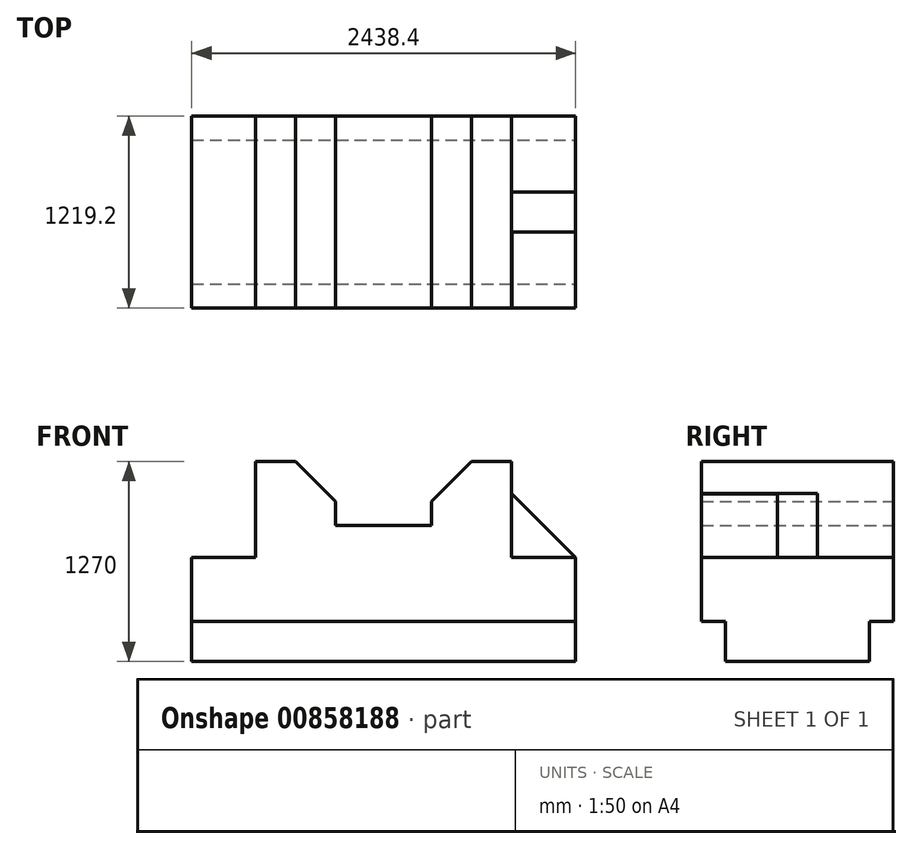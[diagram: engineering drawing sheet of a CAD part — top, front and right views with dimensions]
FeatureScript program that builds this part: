
annotation { "Feature Type Name" : "Feature", "Feature Type Description" : "" }
export const myFeature = defineFeature(function(context is Context, id is Id, definition is map)
    precondition{}
    {
        {
            var Q0;
            Q0=qCreatedBy(makeId("Front.planeOp"),FACE);
            var sketch = newSketch(context, id + "F0", { "sketchPlane" : qUnion([Q0])});
            skLineSegment(sketch, "E0.bottom", {"start": v(-1219.2, 635) * mm, "end": v(1219.2, 635) * mm});
            skLineSegment(sketch, "E0.top", {"start": v(-1219.2, -635) * mm, "end": v(1219.2, -635) * mm});
            skLineSegment(sketch, "E0.left", {"start": v(-1219.2, 635) * mm, "end": v(-1219.2, -635) * mm});
            skLineSegment(sketch, "E0.right", {"start": v(1219.2, 635) * mm, "end": v(1219.2, -635) * mm});
            skPoint(sketch, "E0.middle", {"position": v(0, 0) * mm});
            skLineSegment(sketch, "E1.bottom", {"start": v(1219.2, 635) * mm, "end": v(812.8, 635) * mm});
            skLineSegment(sketch, "E1.top", {"start": v(1219.2, -635) * mm, "end": v(812.8, -635) * mm});
            skLineSegment(sketch, "E1.right", {"start": v(812.8, 635) * mm, "end": v(812.8, -635) * mm});
            skLineSegment(sketch, "E2.top", {"start": v(1219.2, 25.4) * mm, "end": v(812.8, 25.4) * mm});
            skLineSegment(sketch, "E2.left", {"start": v(1219.2, -635) * mm, "end": v(1219.2, 25.4) * mm});
            skLineSegment(sketch, "E3.bottom", {"start": v(812.8, 635) * mm, "end": v(558.8, 635) * mm});
            skLineSegment(sketch, "E3.top", {"start": v(812.8, -635) * mm, "end": v(558.8, -635) * mm});
            skLineSegment(sketch, "E3.right", {"start": v(558.8, 635) * mm, "end": v(558.8, -635) * mm});
            skLineSegment(sketch, "E4.bottom", {"start": v(558.8, -635) * mm, "end": v(304.8, -635) * mm});
            skLineSegment(sketch, "E4.top", {"start": v(558.8, 635) * mm, "end": v(304.8, 635) * mm});
            skLineSegment(sketch, "E4.left", {"start": v(558.8, -635) * mm, "end": v(558.8, 635) * mm});
            skLineSegment(sketch, "E4.right", {"start": v(304.8, -635) * mm, "end": v(304.8, 635) * mm});
            skLineSegment(sketch, "E5.bottom", {"start": v(304.8, -635) * mm, "end": v(-304.8, -635) * mm});
            skLineSegment(sketch, "E5.top", {"start": v(304.8, 635) * mm, "end": v(-304.8, 635) * mm});
            skLineSegment(sketch, "E5.right", {"start": v(-304.8, -635) * mm, "end": v(-304.8, 635) * mm});
            skLineSegment(sketch, "E6.bottom", {"start": v(-1219.2, 635) * mm, "end": v(-812.8, 635) * mm});
            skLineSegment(sketch, "E6.top", {"start": v(-1219.2, -635) * mm, "end": v(-812.8, -635) * mm});
            skLineSegment(sketch, "E6.right", {"start": v(-812.8, 635) * mm, "end": v(-812.8, -635) * mm});
            skLineSegment(sketch, "E7.bottom", {"start": v(-812.8, 635) * mm, "end": v(-558.8, 635) * mm});
            skLineSegment(sketch, "E7.top", {"start": v(-812.8, -635) * mm, "end": v(-558.8, -635) * mm});
            skLineSegment(sketch, "E7.right", {"start": v(-558.8, 635) * mm, "end": v(-558.8, -635) * mm});
            skLineSegment(sketch, "E8.bottom", {"start": v(-812.8, -635) * mm, "end": v(-1219.2, -635) * mm});
            skLineSegment(sketch, "E8.top", {"start": v(-812.8, 25.4) * mm, "end": v(-1219.2, 25.4) * mm});
            skLineSegment(sketch, "E8.left", {"start": v(-812.8, -635) * mm, "end": v(-812.8, 25.4) * mm});
            skLineSegment(sketch, "E8.right", {"start": v(-1219.2, -635) * mm, "end": v(-1219.2, 25.4) * mm});
            skLineSegment(sketch, "E9.top", {"start": v(-812.8, 228.6) * mm, "end": v(-558.8, 228.6) * mm});
            skLineSegment(sketch, "E9.left", {"start": v(-812.8, 635) * mm, "end": v(-812.8, 228.6) * mm});
            skLineSegment(sketch, "E9.right", {"start": v(-558.8, 635) * mm, "end": v(-558.8, 228.6) * mm});
            skLineSegment(sketch, "E10", {"start": v(-558.8, 228.6) * mm, "end": v(304.8, 228.6) * mm});
            skLineSegment(sketch, "E11", {"start": v(-558.8, 228.6) * mm, "end": v(-152.4, 228.6) * mm});
            skLineSegment(sketch, "E12", {"start": v(-558.8, 635) * mm, "end": v(-152.4, 228.6) * mm});
            skLineSegment(sketch, "E13", {"start": v(812.8, 25.4) * mm, "end": v(812.8, 431.8) * mm});
            skLineSegment(sketch, "E14", {"start": v(812.8, 431.8) * mm, "end": v(1219.2, 25.4) * mm});
            skLineSegment(sketch, "E15", {"start": v(304.8, 635) * mm, "end": v(304.8, 381) * mm});
            skLineSegment(sketch, "E16", {"start": v(558.8, 635) * mm, "end": v(304.8, 381) * mm});
            skSolve(sketch);
        }
        {
            var Q0;
            {var subQ5=sQuery(id+"F0.wireOp",EDGE,"E8.top");Q0=makeQuery(id+"F0.imprint","IMPRINT",FACE,{"disambiguationData":[TD([[makeQuery(id+"F0.imprint","IMPRINT",EDGE,{"derivedFrom":subQ5}),1.0]])]});}
            var Q1;
            {var subQ2=sQuery(id+"F0.wireOp",EDGE,"E9.top");Q1=makeQuery(id+"F0.imprint","IMPRINT",FACE,{"disambiguationData":[TD([[makeQuery(id+"F0.imprint","IMPRINT",EDGE,{"derivedFrom":subQ2}),-1.0]])]});}
            var Q2;
            {var subQ5=sQuery(id+"F0.wireOp",EDGE,"E9.top");Q2=makeQuery(id+"F0.imprint","IMPRINT",FACE,{"disambiguationData":[TD([[makeQuery(id+"F0.imprint","IMPRINT",EDGE,{"derivedFrom":subQ5}),1.0]])]});}
            var Q3;
            {var subQ0=sQuery(id+"F0.wireOp",EDGE,"E12");var subQ1=sQuery(id+"F0.wireOp",EDGE,"E5.right");var subQ2=makeQuery(id+"F0.imprint","INTERSECT",VERTEX,{"derivedFrom":[subQ1,subQ0]});Q3=makeQuery(id+"F0.imprint","IMPRINT",FACE,{"disambiguationData":[TD([[makeQuery(id+"F0.imprint","IMPRINT",EDGE,{"disambiguationData":[TD([[subQ2,1.0]])],"derivedFrom":subQ1}),1.0]])]});}
            var Q4;
            {var subQ0=sQuery(id+"F0.wireOp",EDGE,"E5.right");var subQ1=sQuery(id+"F0.wireOp",EDGE,"E0.top");var subQ2=makeQuery(id+"F0.imprint","INTERSECT",VERTEX,{"derivedFrom":[subQ1,subQ0]});Q4=makeQuery(id+"F0.imprint","IMPRINT",FACE,{"disambiguationData":[TD([[makeQuery(id+"F0.imprint","IMPRINT",EDGE,{"disambiguationData":[TD([[subQ2,1.0]])],"derivedFrom":subQ1}),1.0]])]});}
            var Q5;
            {var subQ4=sQuery(id+"F0.wireOp",EDGE,"E5.right");var subQ5=sQuery(id+"F0.wireOp",EDGE,"E0.top");var subQ6=makeQuery(id+"F0.imprint","INTERSECT",VERTEX,{"derivedFrom":[subQ5,subQ4]});Q5=makeQuery(id+"F0.imprint","IMPRINT",FACE,{"disambiguationData":[TD([[makeQuery(id+"F0.imprint","IMPRINT",EDGE,{"disambiguationData":[TD([[subQ6,-1.0]])],"derivedFrom":subQ5}),1.0]])]});}
            var Q6;
            {var subQ4=sQuery(id+"F0.wireOp",EDGE,"E3.right");Q6=makeQuery(id+"F0.imprint","IMPRINT",FACE,{"disambiguationData":[TD([[makeQuery(id+"F0.imprint","IMPRINT",EDGE,{"derivedFrom":subQ4}),-1.0]])]});}
            var Q7;
            {var subQ5=sQuery(id+"F0.wireOp",EDGE,"E3.right");Q7=makeQuery(id+"F0.imprint","IMPRINT",FACE,{"disambiguationData":[TD([[makeQuery(id+"F0.imprint","IMPRINT",EDGE,{"derivedFrom":subQ5}),1.0]])]});}
            var Q8;
            {var subQ0=sQuery(id+"F0.wireOp",EDGE,"E2.top");Q8=makeQuery(id+"F0.imprint","IMPRINT",FACE,{"disambiguationData":[TD([[makeQuery(id+"F0.imprint","IMPRINT",EDGE,{"derivedFrom":subQ0}),-1.0]])]});}
            var Q9;
            {var subQ5=sQuery(id+"F0.wireOp",EDGE,"E2.top");Q9=makeQuery(id+"F0.imprint","IMPRINT",FACE,{"disambiguationData":[TD([[makeQuery(id+"F0.imprint","IMPRINT",EDGE,{"derivedFrom":subQ5}),1.0]])]});}
            extrude(context, id + "F1", {"entities" : qUnion([Q0, Q1, Q2, Q3, Q4, Q5, Q6, Q7, Q8, Q9]), "depth" : 1219.2 * mm, "offsetDistance" : 25.4 * mm});
        }
        {
            var Q0;
            Q0=makeQuery(id+"F1.opExtrude","SWEPT_FACE",FACE,{"disambiguationData":[OSD([sQuery(id+"F0.wireOp",EDGE,"E0.right")])]});
            var sketch = newSketch(context, id + "F2", { "sketchPlane" : qUnion([Q0])});
            skLineSegment(sketch, "E17.bottom", {"start": v(-1219.2, -635) * mm, "end": v(-1066.8, -635) * mm});
            skLineSegment(sketch, "E17.top", {"start": v(-1219.2, -381) * mm, "end": v(-1066.8, -381) * mm});
            skLineSegment(sketch, "E17.left", {"start": v(-1219.2, -635) * mm, "end": v(-1219.2, -381) * mm});
            skLineSegment(sketch, "E17.right", {"start": v(-1066.8, -635) * mm, "end": v(-1066.8, -381) * mm});
            skLineSegment(sketch, "E18.bottom", {"start": v(0, -635) * mm, "end": v(-152.4, -635) * mm});
            skLineSegment(sketch, "E18.top", {"start": v(0, -381) * mm, "end": v(-152.4, -381) * mm});
            skLineSegment(sketch, "E18.left", {"start": v(0, -635) * mm, "end": v(0, -381) * mm});
            skLineSegment(sketch, "E18.right", {"start": v(-152.4, -635) * mm, "end": v(-152.4, -381) * mm});
            skSolve(sketch);
        }
        {
            var Q0;
            Q0=makeQuery(id+"F2.imprint","IMPRINT",FACE,{"disambiguationData":[TD([[makeQuery(id+"F2.imprint","IMPRINT",EDGE,{"derivedFrom":sQuery(id+"F2.wireOp",EDGE,"E17.bottom")}),1.0]])]});
            var Q1;
            Q1=makeQuery(id+"F2.imprint","IMPRINT",FACE,{"disambiguationData":[TD([[makeQuery(id+"F2.imprint","IMPRINT",EDGE,{"derivedFrom":sQuery(id+"F2.wireOp",EDGE,"E18.bottom")}),1.0]])]});
            extrude(context, id + "F3", {"entities" : qUnion([Q0, Q1]), "operationType" : NewBodyOperationType.REMOVE, "oppositeDirection" : true, "depth" : 2438.4 * mm, "offsetDistance" : 25.4 * mm});
        }
        {
            var Q0;
            Q0=makeQuery(id+"F1.opExtrude","SWEPT_FACE",FACE,{"disambiguationData":[OSD([sQuery(id+"F0.wireOp",EDGE,"E0.right")])]});
            var sketch = newSketch(context, id + "F4", { "sketchPlane" : qUnion([Q0])});
            skLineSegment(sketch, "E19.bottom", {"start": v(-1219.2, 25.4) * mm, "end": v(-736.6, 25.4) * mm});
            skLineSegment(sketch, "E19.top", {"start": v(-1219.2, 430.42) * mm, "end": v(-736.6, 430.42) * mm});
            skLineSegment(sketch, "E19.left", {"start": v(-1219.2, 25.4) * mm, "end": v(-1219.2, 430.42) * mm});
            skLineSegment(sketch, "E19.right", {"start": v(-736.6, 25.4) * mm, "end": v(-736.6, 430.42) * mm});
            skLineSegment(sketch, "E20.bottom", {"start": v(0, 25.4) * mm, "end": v(-482.6, 25.4) * mm});
            skLineSegment(sketch, "E20.top", {"start": v(0, 431.9) * mm, "end": v(-482.6, 431.9) * mm});
            skLineSegment(sketch, "E20.left", {"start": v(0, 25.4) * mm, "end": v(0, 431.9) * mm});
            skLineSegment(sketch, "E20.right", {"start": v(-482.6, 25.4) * mm, "end": v(-482.6, 431.9) * mm});
            skSolve(sketch);
        }
        {
            var Q0;
            Q0=makeQuery(id+"F4.imprint","IMPRINT",FACE,{"disambiguationData":[TD([[makeQuery(id+"F4.imprint","IMPRINT",EDGE,{"derivedFrom":sQuery(id+"F4.wireOp",EDGE,"E20.bottom")}),1.0]])]});
            var Q1;
            Q1=makeQuery(id+"F4.imprint","IMPRINT",FACE,{"disambiguationData":[TD([[makeQuery(id+"F4.imprint","IMPRINT",EDGE,{"derivedFrom":sQuery(id+"F4.wireOp",EDGE,"E19.bottom")}),1.0]])]});
            extrude(context, id + "F5", {"entities" : qUnion([Q0, Q1]), "operationType" : NewBodyOperationType.REMOVE, "oppositeDirection" : true, "depth" : 406.4 * mm, "offsetDistance" : 25.4 * mm});
        }
    });
